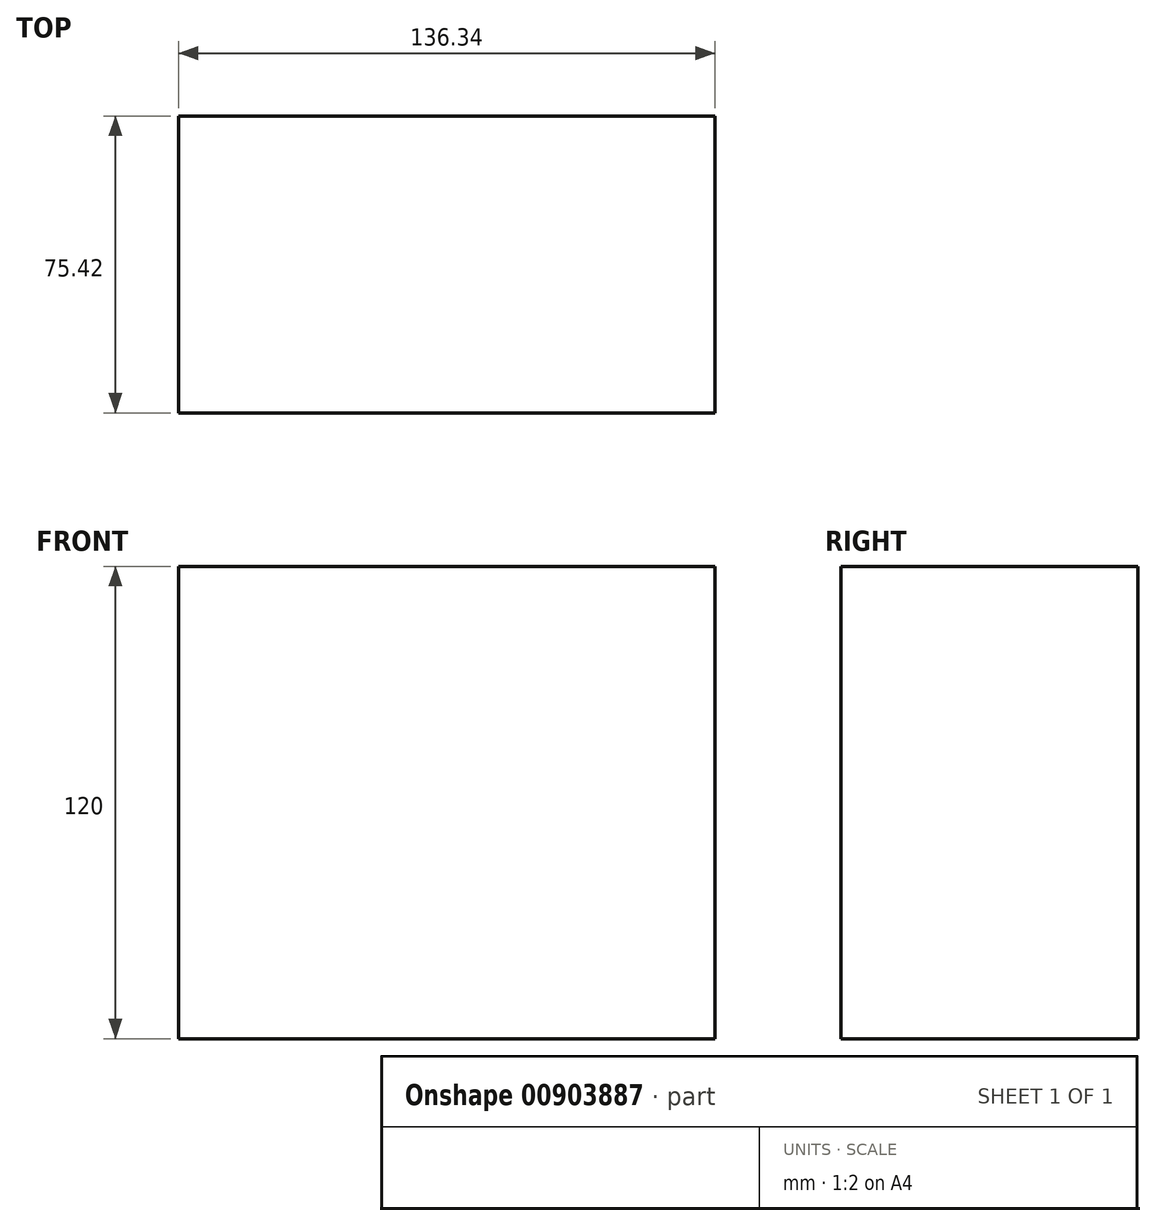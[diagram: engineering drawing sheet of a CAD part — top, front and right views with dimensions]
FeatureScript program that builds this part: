
annotation { "Feature Type Name" : "Feature", "Feature Type Description" : "" }
export const myFeature = defineFeature(function(context is Context, id is Id, definition is map)
    precondition{}
    {
        {
            var Q0;
            Q0=qCreatedBy(makeId("Top.planeOp"),FACE);
            var sketch = newSketch(context, id + "F0", { "sketchPlane" : qUnion([Q0])});
            skLineSegment(sketch, "E0.bottom", {"start": v(-68.17, 35.87) * mm, "end": v(68.17, 35.87) * mm});
            skLineSegment(sketch, "E0.top", {"start": v(-68.17, -39.55) * mm, "end": v(68.17, -39.55) * mm});
            skLineSegment(sketch, "E0.left", {"start": v(-68.17, 35.87) * mm, "end": v(-68.17, -39.55) * mm});
            skLineSegment(sketch, "E0.right", {"start": v(68.17, 35.87) * mm, "end": v(68.17, -39.55) * mm});
            skPoint(sketch, "E0.middle", {"position": v(0, -1.84) * mm});
            skSolve(sketch);
        }
        {
            var Q0;
            Q0 = qSketchRegion(id + "F0", true);
            extrude(context, id + "F1", {"entities" : qUnion([Q0]), "depth" : 120 * mm, "offsetDistance" : 25 * mm});
        }
    });
